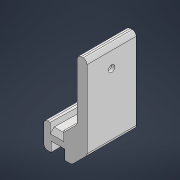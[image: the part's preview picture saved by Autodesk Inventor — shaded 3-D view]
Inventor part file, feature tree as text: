
AUTODESK INVENTOR PART (.ipt)
format: ipt  version: 2022 (Build 260153000, 153)  size: 173,056 bytes
history: native  units: mm
features: other x8, reference x6, sketch x4, extrude x3, chamfer x3, hole x1, fillet x1, projected_geometry x1
ambient origin geometry x8: Origin, YZ Plane, XZ Plane, XY Plane, X Axis, Y Axis, Z Axis, Center Point
bodies: Solid1 (feature_tree)
feature tree (27):
  extrude  "Extrusion1"  Depth=5.0mm
  extrude  "Extrusion2"  Depth=2.0mm
  extrude  "Extrusion3"  Depth=25.0mm
  chamfer  "Chamfer1"  Distance=25.0mm
  chamfer  "Chamfer3"  Distance=3.0mm
  hole  "Hole1"  [1 undecoded]
  fillet  "Fillet3"  Radius=2.0mm
  chamfer  "Chamfer4"  Distance=2.0mm Angle=45.0deg
  sketch  "Sketch1"  dims[d0=5.0mm d1=15.0mm]
  sketch  "Sketch2"  dims[d2=4.0mm d3=2.0mm]
  reference  "Reference1"
  reference  "Reference2"
  sketch  "Sketch3"  dims[d4=40.85mm d5=6.0mm d6=25.0mm d7=0.0mm]
  projected_geometry  "Projected Loop1"
  reference  "Reference3"
  reference  "Reference4"
  reference  "Reference5"
  sketch  "Sketch5"  dims[d8=7.0mm d9=3.0mm d10=0.0mm d13=3.0mm d14=0.0mm d16=7.75mm d17=2.0mm d18=45.0deg d24=6.0mm d25=2.0mm d26=45.0deg d27=3.4mm d28=6.0mm d29=6.5mm d30=3.4mm d31=90.0deg d32=8.0mm d33=20.594885mm d34=2.0mm d35=2.0mm d36=2.0mm d37=45.0deg d38=7.0mm]
  reference  "Reference6"
  parser-record x1  (decoder bookkeeping rows leaked as tree rows — omitted from the tree; the rows remain in map.json)
  other  "Bibble0.iam"
  other  "603 Bearing:10"
  other  "603 Bearing:14"
  other  "603 Bearing:15"
  other  "2020 Y Axis:5"
  other  "603 Bearing:12"
  other  "2020 X Axis:3"
note: 1 required parameter value undecoded (feature->parameter linkage not recoverable at this tier; creation-order binding heuristic only, values carry confidence <= 0.55)
note: 1 file-system path scrubbed to <path> (originals preserved in map.json)
